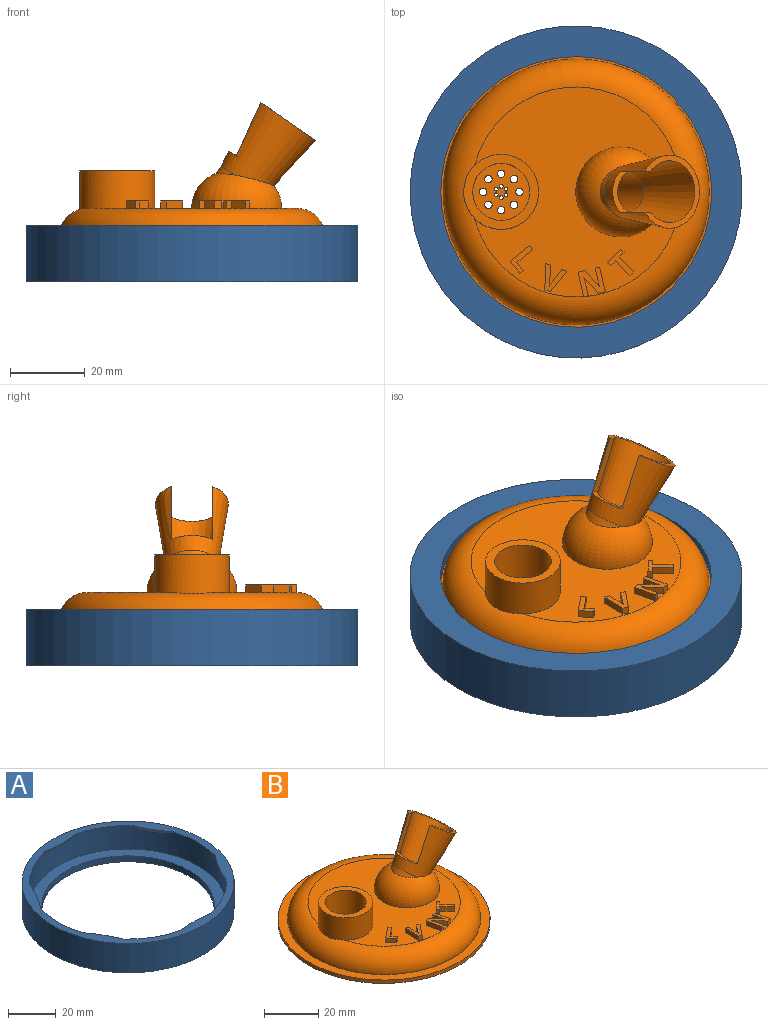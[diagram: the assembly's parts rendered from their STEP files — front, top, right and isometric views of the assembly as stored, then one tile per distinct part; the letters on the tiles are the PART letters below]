
ASSEMBLY  parts=2 mates=1
PART A: 24 faces, bbox 88.6x88.6x15 mm
  f0: cylinder r=44.3mm len=88.6mm, axis (0,0,-1), area 4175.2mm2, adj f1,f3
  f1: plane 88.6x88.6mm, normal (0,0,-1), area 2071.2mm2, adj f0,f17
  f2: cylinder r=41.1mm len=82.2mm, axis (0,0,-1), area 2930.5mm2, adj f3,f4,f5,f6,f7,f8,f9,f10
  f3: plane 88.6x88.6mm, normal (0,0,1), area 973.9mm2, adj f0,f2,f5,f7,f9,f11,f13,f15
  f4: plane 82.2x82.2mm, normal (0,0,1), area 1212.7mm2, adj f2,f17
  f5: cylinder r=67.52mm len=18mm, axis (0,0,1), area 9mm2, adj f2,f3,f22
  f6: plane 4.5x0.1mm, normal (0,0,-1), area 0.3mm2, adj f2,f22
  f7: cylinder r=67.52mm len=15.59mm, axis (0,0,1), area 9mm2, adj f2,f3,f21
  f8: plane 3.9x2.25mm, normal (0,0,-1), area 0.3mm2, adj f2,f21
  f9: cylinder r=67.52mm len=15.59mm, axis (0,0,1), area 9mm2, adj f2,f3,f20
  f10: plane 3.9x2.25mm, normal (0,0,-1), area 0.3mm2, adj f2,f20
  f11: cylinder r=67.52mm len=18mm, axis (0,0,1), area 9mm2, adj f2,f3,f19
  f12: plane 4.5x0.1mm, normal (0,0,-1), area 0.3mm2, adj f2,f19
  f13: cylinder r=67.52mm len=15.59mm, axis (0,0,1), area 9mm2, adj f2,f3,f18
  f14: plane 3.9x2.25mm, normal (0,0,-1), area 0.3mm2, adj f2,f18
  f15: cylinder r=67.52mm len=15.59mm, axis (0,0,1), area 9mm2, adj f2,f3,f23
  f16: plane 3.9x2.25mm, normal (0,0,-1), area 0.3mm2, adj f2,f23
  f17: cylinder r=36.1mm len=72.2mm, axis (0,0,1), area 680.5mm2, adj f1,f4
  f18: cone r=67.52mm half-angle=45deg, axis (0,0,1), area 26.8mm2, adj f2,f13,f14
  f19: cone r=67.52mm half-angle=45deg, axis (0,0,1), area 26.8mm2, adj f2,f11,f12
  f20: cone r=67.52mm half-angle=45deg, axis (0,0,1), area 26.8mm2, adj f2,f9,f10
  f21: cone r=67.52mm half-angle=45deg, axis (0,0,1), area 26.8mm2, adj f2,f7,f8
  f22: cone r=67.52mm half-angle=45deg, axis (0,0,1), area 26.8mm2, adj f2,f5,f6
  f23: cone r=67.52mm half-angle=45deg, axis (0,0,1), area 26.8mm2, adj f2,f15,f16
PART B: 74 faces, bbox 78x78x44.6 mm
  f0: plane 2x0.84mm, normal (0.71,0.7,0), area 2.4mm2, adj f1,f7,f8,f27
  f1: plane 3.58x3.55mm, normal (-0.7,0.71,0), area 10.1mm2, adj f0,f2,f8,f27
  f2: plane 2x0.84mm, normal (-0.71,-0.7,0), area 2.4mm2, adj f1,f3,f8,f27
  f3: plane 2x1.29mm, normal (0.7,-0.71,0), area 3.6mm2, adj f2,f4,f8,f27
  f4: plane 3.91x3.87mm, normal (-0.71,-0.7,0), area 11mm2, adj f3,f5,f8,f27
  f5: plane 2x1.01mm, normal (0.7,-0.71,0), area 2.8mm2, adj f4,f6,f8,f27
  f6: plane 3.91x3.87mm, normal (0.71,0.7,0), area 11mm2, adj f5,f7,f8,f27
  f7: plane 2x1.29mm, normal (0.7,-0.71,0), area 3.6mm2, adj f0,f6,f8,f27
  f8: plane 7.02x6.99mm, normal (0,0,1), area 13.7mm2, adj f0,f1,f2,f3,f4,f5,f6,f7
  f9: plane 2.1x2mm, normal (0.77,0.63,0), area 5.4mm2, adj f10,f14,f15,f27
  f10: plane 4.26x3.49mm, normal (0.63,-0.77,0), area 11mm2, adj f9,f11,f15,f27
  f11: plane 2x1.1mm, normal (0.77,0.63,0), area 2.8mm2, adj f10,f12,f15,f27
  f12: plane 5.17x4.23mm, normal (-0.63,0.77,0), area 13.4mm2, adj f11,f13,f15,f27
  f13: plane 3.19x2.61mm, normal (-0.77,-0.63,0), area 8.2mm2, adj f12,f14,f15,f27
  f14: plane 2x0.9mm, normal (0.63,-0.77,0), area 2.3mm2, adj f9,f13,f15,f27
  f15: plane 7.42x6.06mm, normal (0,0,1), area 12.6mm2, adj f9,f10,f11,f12,f13,f14
  f16: extruded ~2x0.66mm, area 1.3mm2, adj f17,f25,f26,f27
  f17: extruded ~2x0.84mm, area 1.7mm2, adj f16,f18,f26,f27
  f18: plane 4.16x2mm, normal (1,-0.05,0), area 8.3mm2, adj f17,f19,f26,f27
  f19: plane 2x1.34mm, normal (0.35,0.94,0), area 2.9mm2, adj f18,f20,f26,f27
  f20: plane 7.05x2mm, normal (-1,0.03,0), area 14.1mm2, adj f19,f21,f26,f27
  f21: plane 2x1.45mm, normal (-0.35,-0.94,0), area 3.1mm2, adj f20,f22,f26,f27
  f22: plane 5.47x4.45mm, normal (0.78,-0.63,0), area 14.1mm2, adj f21,f23,f26,f27
  f23: plane 2x1.34mm, normal (0.35,0.94,0), area 2.9mm2, adj f22,f24,f26,f27
  f24: plane 3.29x2.57mm, normal (-0.79,0.62,0), area 8.3mm2, adj f23,f25,f26,f27
  f25: extruded ~2x1.26mm, area 3mm2, adj f16,f24,f26,f27
  f26: plane 7.58x5.9mm, normal (0,0,1), area 17.2mm2, adj f16,f17,f18,f19,f20,f21,f22,f23
  f27: plane 56x55.1mm, normal (0,0,1), area 1647.3mm2, adj f0,f1,f2,f3,f4,f5,f6,f7
  f28: plane 3.08x2mm, normal (-0.97,-0.22,0), area 6.3mm2, adj f27,f29,f41,f42
  f29: extruded ~2x1.78mm, area 3.7mm2, adj f27,f28,f30,f42
  f30: plane 2x0.03mm, normal (-0.22,0.97,0), area 0.1mm2, adj f27,f29,f31,f42
  f31: plane 4.23x3.94mm, normal (0.73,0.68,0), area 11.6mm2, adj f27,f30,f32,f42
  f32: plane 2x1.74mm, normal (-0.22,0.97,0), area 3.6mm2, adj f27,f31,f33,f42
  f33: plane 6.51x2mm, normal (-0.97,-0.22,0), area 13.4mm2, adj f27,f32,f34,f42
  f34: plane 2x1.23mm, normal (0.22,-0.97,0), area 2.5mm2, adj f27,f33,f35,f42
  f35: plane 3.06x2mm, normal (0.97,0.22,0), area 6.3mm2, adj f27,f34,f36,f42
  f36: extruded ~2x1.84mm, area 3.8mm2, adj f27,f35,f37,f42
  f37: plane 2x0.04mm, normal (0.22,-0.97,0), area 0.1mm2, adj f27,f36,f38,f42
  f38: plane 4.28x3.96mm, normal (-0.73,-0.68,0), area 11.7mm2, adj f27,f37,f39,f42
  f39: plane 2x1.75mm, normal (0.22,-0.97,0), area 3.6mm2, adj f27,f38,f40,f42
  f40: plane 6.51x2mm, normal (0.97,0.22,0), area 13.4mm2, adj f27,f39,f41,f42
  f41: plane 2x1.24mm, normal (-0.22,0.97,0), area 2.5mm2, adj f27,f28,f40,f42
  f42: plane 7.83x7.26mm, normal (0,0,1), area 25.3mm2, adj f28,f29,f30,f31,f32,f33,f34,f35
  f43: cone r=7mm half-angle=7.8deg, axis (0.57,0,0.82), area 804mm2, adj f44,f67,f68,f71,f72,f73
  f44: torus R=2mm, axis (0,0,1), area 646.5mm2, adj f27,f43,f68
  f45: torus R=28mm, axis (0,0,1), area 2406.2mm2, adj f27,f47,f50
  f46: cylinder r=39mm len=78mm, axis (0,0,-1), area 367.6mm2, adj f47,f48
  f47: plane 78x78mm, normal (0,0,1), area 819.2mm2, adj f45,f46
  f48: plane 78x78mm, normal (0,0,-1), area 4632.5mm2, adj f46,f53,f54,f55,f56,f57,f58,f59
  f49: plane 20x20mm, normal (0,0,1), area 132.7mm2, adj f50,f52
  f50: cylinder r=10mm len=20mm, axis (0,0,-1), area 630.6mm2, adj f27,f45,f49
  f51: plane 15.2x15.2mm, normal (0,0,1), area 151.6mm2, adj f52,f53,f54,f55,f56,f57,f58,f59
  f52: cylinder r=7.6mm len=17mm, axis (0,0,1), area 811.8mm2, adj f49,f51
  f53: cylinder r=0.5mm len=2mm, axis (0,0,1), area 6.3mm2, adj f48,f51
  f54: cylinder r=1mm len=2mm, axis (0,0,1), area 12.6mm2, adj f48,f51
  f55: cylinder r=1mm len=2mm, axis (0,0,1), area 12.6mm2, adj f48,f51
  f56: cylinder r=1mm len=2mm, axis (0,0,1), area 12.6mm2, adj f48,f51
  f57: cylinder r=1mm len=2mm, axis (0,0,1), area 12.6mm2, adj f48,f51
  f58: cylinder r=1mm len=2mm, axis (0,0,1), area 12.6mm2, adj f48,f51
  f59: cylinder r=0.5mm len=2mm, axis (0,0,1), area 6.3mm2, adj f48,f51
  f60: cylinder r=0.5mm len=2mm, axis (0,0,1), area 6.3mm2, adj f48,f51
  f61: cylinder r=0.5mm len=2mm, axis (0,0,1), area 6.3mm2, adj f48,f51
  f62: cylinder r=0.5mm len=2mm, axis (0,0,1), area 6.3mm2, adj f48,f51
  f63: cylinder r=0.5mm len=2mm, axis (0,0,1), area 6.3mm2, adj f48,f51
  f64: cylinder r=1mm len=2mm, axis (0,0,1), area 12.6mm2, adj f48,f51
  f65: cylinder r=1mm len=2mm, axis (0,0,1), area 12.6mm2, adj f48,f51
  f66: cylinder r=1mm len=2mm, axis (0,0,1), area 12.6mm2, adj f48,f51
  f67: plane 19.5x14.59mm, normal (0.57,0,0.82), area 67mm2, adj f43,f70,f72,f73
  f68: cylinder r=7mm len=12.7mm, axis (0.57,0,0.82), area 23.8mm2, adj f43,f44
  f69: cylinder r=5.5mm len=25.8mm, axis (0.57,0,0.82), area 687.2mm2, adj f48,f70
  f70: cone r=5.5mm half-angle=7.8deg, axis (0.57,0,0.82), area 677mm2, adj f67,f69,f71,f72,f73
  f71: plane 11.02x4.32mm, normal (0.46,0,0.89), area 19mm2, adj f43,f70,f72,f73
  f72: plane 15.27x8.11mm, normal (0,-1,0), area 32.3mm2, adj f43,f67,f70,f71
  f73: plane 15.29x8.1mm, normal (0,1,0), area 32.5mm2, adj f43,f67,f70,f71
PLACE A rot(axis=(0,-1,0),180deg) t=(20.85,0,21.79)mm
PLACE B t=(20.85,0,17.29)mm
MATE planar B.f46 <-> A.f0  axis (0,0,1) through (20.85,0,18.79)mm
